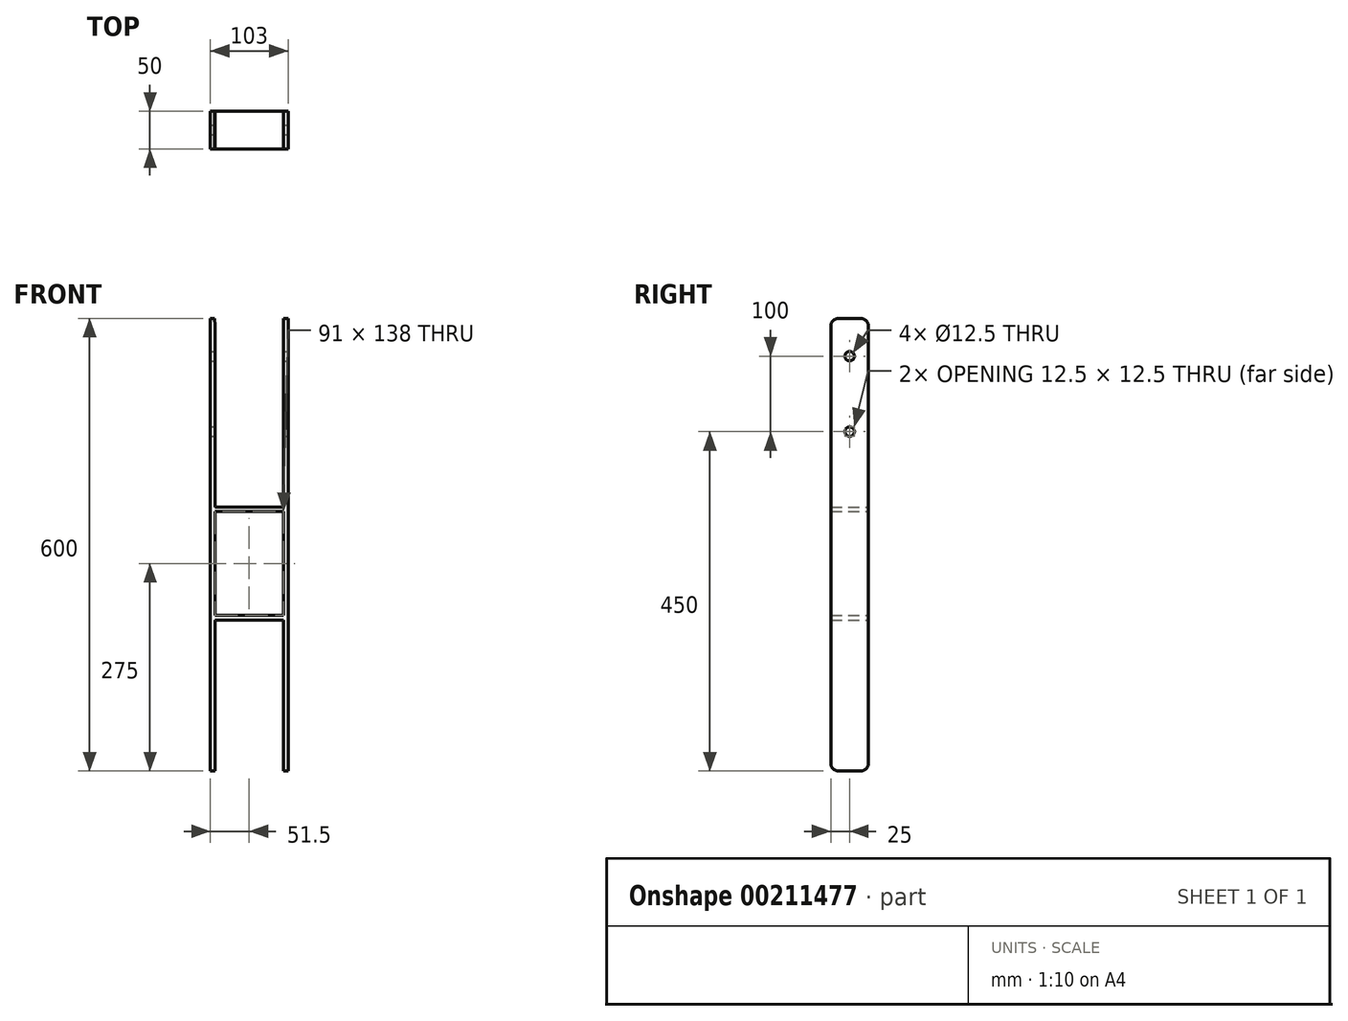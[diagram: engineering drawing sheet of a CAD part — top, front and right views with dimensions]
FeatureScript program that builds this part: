
annotation { "Feature Type Name" : "Feature", "Feature Type Description" : "" }
export const myFeature = defineFeature(function(context is Context, id is Id, definition is map)
    precondition{}
    {
        {
            var Q0;
            Q0=qCreatedBy(makeId("Front.planeOp"),FACE);
            var sketch = newSketch(context, id + "F0", { "sketchPlane" : qUnion([Q0])});
            skLineSegment(sketch, "E0", {"start": v(-200.62, 0) * mm, "end": v(200.75, 0) * mm, "construction": true});
            skLineSegment(sketch, "E1", {"start": v(0, -177.39) * mm, "end": v(0, 159.8) * mm, "construction": true});
            skLineSegment(sketch, "E2", {"start": v(-45.5, 0) * mm, "end": v(45.5, 0) * mm});
            skLineSegment(sketch, "E3", {"start": v(45.5, 0) * mm, "end": v(45.5, 250) * mm});
            skLineSegment(sketch, "E4", {"start": v(45.5, 250) * mm, "end": v(51.5, 250) * mm});
            skLineSegment(sketch, "E5", {"start": v(51.5, 250) * mm, "end": v(51.5, -350) * mm});
            skLineSegment(sketch, "E6", {"start": v(51.5, -350) * mm, "end": v(45.5, -350) * mm});
            skLineSegment(sketch, "E7", {"start": v(45.5, -350) * mm, "end": v(45.5, -150) * mm});
            skLineSegment(sketch, "E8", {"start": v(45.5, -150) * mm, "end": v(-45.5, -150) * mm});
            skLineSegment(sketch, "E9", {"start": v(-45.5, -150) * mm, "end": v(-45.5, -350) * mm});
            skLineSegment(sketch, "E10", {"start": v(-45.5, -350) * mm, "end": v(-51.5, -350) * mm});
            skLineSegment(sketch, "E11", {"start": v(-51.5, -350) * mm, "end": v(-51.5, 250) * mm});
            skLineSegment(sketch, "E12", {"start": v(-51.5, 250) * mm, "end": v(-45.7, 250) * mm});
            skLineSegment(sketch, "E13", {"start": v(-45.7, 250) * mm, "end": v(-45.5, 0) * mm});
            skLineSegment(sketch, "E14.bottom", {"start": v(-45.5, -6) * mm, "end": v(45.5, -6) * mm});
            skLineSegment(sketch, "E14.top", {"start": v(-45.5, -144) * mm, "end": v(45.5, -144) * mm});
            skLineSegment(sketch, "E14.left", {"start": v(-45.5, -6) * mm, "end": v(-45.5, -144) * mm});
            skLineSegment(sketch, "E14.right", {"start": v(45.5, -6) * mm, "end": v(45.5, -144) * mm});
            skSolve(sketch);
        }
        {
            var Q0;
            Q0=qSketchRegion(id+"F0",true);
            extrude(context, id + "F1", {"entities" : qUnion([Q0]), "depth" : 50 * mm, "symmetric" : true});
        }
        {
            var Q0;
            Q0=makeQuery(id+"F1.opExtrude","CAP_EDGE",EDGE,{"disambiguationData":[OSD([sQuery(id+"F0.wireOp",EDGE,"E4")])],"isStart":false});
            var Q1;
            Q1=makeQuery(id+"F1.opExtrude","CAP_EDGE",EDGE,{"disambiguationData":[OSD([sQuery(id+"F0.wireOp",EDGE,"E4")])],"isStart":true});
            var Q2;
            Q2=makeQuery(id+"F1.opExtrude","CAP_EDGE",EDGE,{"disambiguationData":[OSD([sQuery(id+"F0.wireOp",EDGE,"E12")])],"isStart":false});
            var Q3;
            Q3=makeQuery(id+"F1.opExtrude","CAP_EDGE",EDGE,{"disambiguationData":[OSD([sQuery(id+"F0.wireOp",EDGE,"E12")])],"isStart":true});
            var Q4;
            Q4=makeQuery(id+"F1.opExtrude","CAP_EDGE",EDGE,{"disambiguationData":[OSD([sQuery(id+"F0.wireOp",EDGE,"E6")])],"isStart":false});
            var Q5;
            Q5=makeQuery(id+"F1.opExtrude","CAP_EDGE",EDGE,{"disambiguationData":[OSD([sQuery(id+"F0.wireOp",EDGE,"E10")])],"isStart":false});
            var Q6;
            Q6=makeQuery(id+"F1.opExtrude","CAP_EDGE",EDGE,{"disambiguationData":[OSD([sQuery(id+"F0.wireOp",EDGE,"E6")])],"isStart":true});
            var Q7;
            Q7=makeQuery(id+"F1.opExtrude","CAP_EDGE",EDGE,{"disambiguationData":[OSD([sQuery(id+"F0.wireOp",EDGE,"E10")])],"isStart":true});
            fillet(context, id + "F2", {"entities" : qUnion([Q0, Q1, Q2, Q3, Q4, Q5, Q6, Q7]), "radius" : 10 * mm, "tangentPropagation" : true, "allowEdgeOverflow" : false});
        }
        {
            var Q0;
            Q0=makeQuery(id+"F1.opExtrude","SWEPT_FACE",FACE,{"disambiguationData":[OSD([sQuery(id+"F0.wireOp",EDGE,"E5")])]});
            var sketch = newSketch(context, id + "F3", { "sketchPlane" : qUnion([Q0])});
            skLineSegment(sketch, "E15", {"start": v(0, 0) * mm, "end": v(0, 250) * mm, "construction": true});
            skCircle(sketch, "E16", {"center": v(0, 200) * mm, "radius": 6.25 * mm});
            skCircle(sketch, "E17", {"center": v(0, 100) * mm, "radius": 6.25 * mm});
            skSolve(sketch);
        }
        {
            var Q0;
            Q0=qSketchRegion(id+"F3",true);
            extrude(context, id + "F4", {"entities" : qUnion([Q0]), "operationType" : NewBodyOperationType.REMOVE, "endBound" : BoundingType.THROUGH_ALL, "oppositeDirection" : true, "depth" : 25 * mm});
        }
    });
